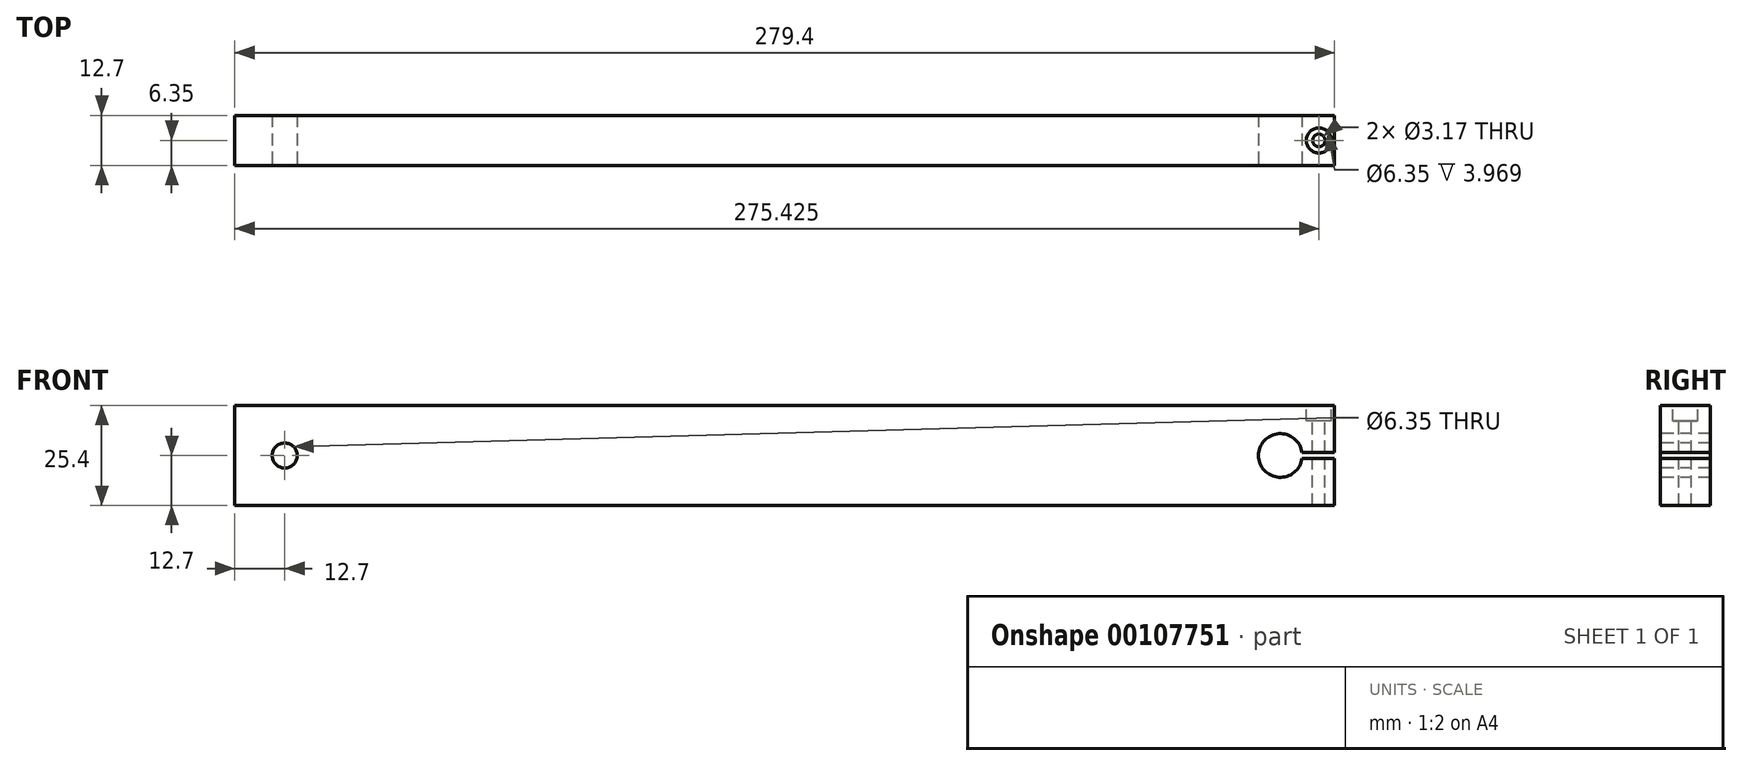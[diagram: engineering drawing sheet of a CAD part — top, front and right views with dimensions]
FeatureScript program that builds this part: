
annotation { "Feature Type Name" : "Feature", "Feature Type Description" : "" }
export const myFeature = defineFeature(function(context is Context, id is Id, definition is map)
    precondition{}
    {
        {
            var Q0;
            Q0=qCreatedBy(makeId("Front.planeOp"),FACE);
            var sketch = newSketch(context, id + "F0", { "sketchPlane" : qUnion([Q0])});
            skLineSegment(sketch, "E0.bottom", {"start": v(139.7, -12.7) * mm, "end": v(-139.7, -12.7) * mm});
            skLineSegment(sketch, "E0.top", {"start": v(139.7, 12.7) * mm, "end": v(-139.7, 12.7) * mm});
            skLineSegment(sketch, "E0.left", {"start": v(139.7, -12.7) * mm, "end": v(139.7, 12.7) * mm});
            skLineSegment(sketch, "E0.right", {"start": v(-139.7, -12.7) * mm, "end": v(-139.7, 12.7) * mm});
            skPoint(sketch, "E0.middle", {"position": v(0, 0) * mm});
            skSolve(sketch);
        }
        {
            var Q0;
            Q0 = qSketchRegion(id + "F0", true);
            extrude(context, id + "F1", {"entities" : qUnion([Q0]), "depth" : 12.7 * mm});
        }
        {
            var Q0;
            Q0=makeQuery(id+"F1.opExtrude","CAP_FACE",FACE,{"disambiguationData":[OSD([sQuery(id+"F0.wireOp",EDGE,"E0.bottom"),sQuery(id+"F0.wireOp",EDGE,"E0.top"),sQuery(id+"F0.wireOp",EDGE,"E0.left"),sQuery(id+"F0.wireOp",EDGE,"E0.right")])],"isStart":false});
            var sketch = newSketch(context, id + "F2", { "sketchPlane" : qUnion([Q0])});
            skCircle(sketch, "E1", {"center": v(-127, 0) * mm, "radius": 3.18 * mm});
            skLineSegment(sketch, "E2", {"start": v(-130.18, 0) * mm, "end": v(-127, 0) * mm});
            skPoint(sketch, "E3.orphan", {"position": v(-139.7, 0) * mm});
            skPoint(sketch, "E4.orphan", {"position": v(139.7, 0) * mm});
            skArc(sketch, "E5", {"start": v(131.45, 0.8) * mm, "mid": v(120.4, 0) * mm, "end": v(131.45, -0.8) * mm});
            skPoint(sketch, "E6.end.orphan", {"position": v(139.7, 0.8) * mm});
            skPoint(sketch, "E7.end.orphan", {"position": v(139.7, -0.8) * mm});
            skLineSegment(sketch, "E8", {"start": v(139.7, 0.8) * mm, "end": v(131.45, 0.8) * mm});
            skLineSegment(sketch, "E9", {"start": v(139.7, -0.8) * mm, "end": v(131.45, -0.8) * mm});
            skPoint(sketch, "E10.end.orphan", {"position": v(126.96, 0) * mm});
            skSolve(sketch);
        }
        {
            var Q0;
            Q0=makeQuery(id+"F1.opExtrude","SWEPT_FACE",FACE,{"disambiguationData":[OSD([sQuery(id+"F0.wireOp",EDGE,"E0.top")])]});
            var sketch = newSketch(context, id + "F3", { "sketchPlane" : qUnion([Q0])});
            skPoint(sketch, "E11.endSnap0", {"position": v(139.7, -6.35) * mm});
            skCircle(sketch, "E12", {"center": v(135.72, -6.35) * mm, "radius": 1.59 * mm});
            skSolve(sketch);
        }
        {
            var Q0;
            Q0 = qSketchRegion(id + "F3", true);
            extrude(context, id + "F4", {"entities" : qUnion([Q0]), "operationType" : NewBodyOperationType.REMOVE, "endBound" : BoundingType.THROUGH_ALL, "oppositeDirection" : true, "depth" : 25.4 * mm});
        }
        {
            var Q0;
            Q0=makeQuery(id+"F1.opExtrude","SWEPT_FACE",FACE,{"disambiguationData":[OSD([sQuery(id+"F0.wireOp",EDGE,"E0.top")])]});
            var sketch = newSketch(context, id + "F5", { "sketchPlane" : qUnion([Q0])});
            skCircle(sketch, "E13", {"center": v(135.72, -6.35) * mm, "radius": 3.18 * mm});
            skSolve(sketch);
        }
        {
            var Q0;
            Q0 = qSketchRegion(id + "F5", true);
            extrude(context, id + "F6", {"entities" : qUnion([Q0]), "operationType" : NewBodyOperationType.REMOVE, "oppositeDirection" : true, "depth" : 3.97 * mm});
        }
        {
            var Q0;
            Q0 = qSketchRegion(id + "F2", true);
            var Q1;
            Q1=makeQuery(id+"F2.imprint","IMPRINT",FACE,{"disambiguationData":[TD([[makeQuery(id+"F2.imprint","IMPRINT",EDGE,{"derivedFrom":sQuery(id+"F2.wireOp",EDGE,"E5")}),1.0]])]});
            extrude(context, id + "F7", {"entities" : qUnion([Q0, Q1]), "operationType" : NewBodyOperationType.REMOVE, "endBound" : BoundingType.THROUGH_ALL, "oppositeDirection" : true, "depth" : 25.4 * mm});
        }
    });
